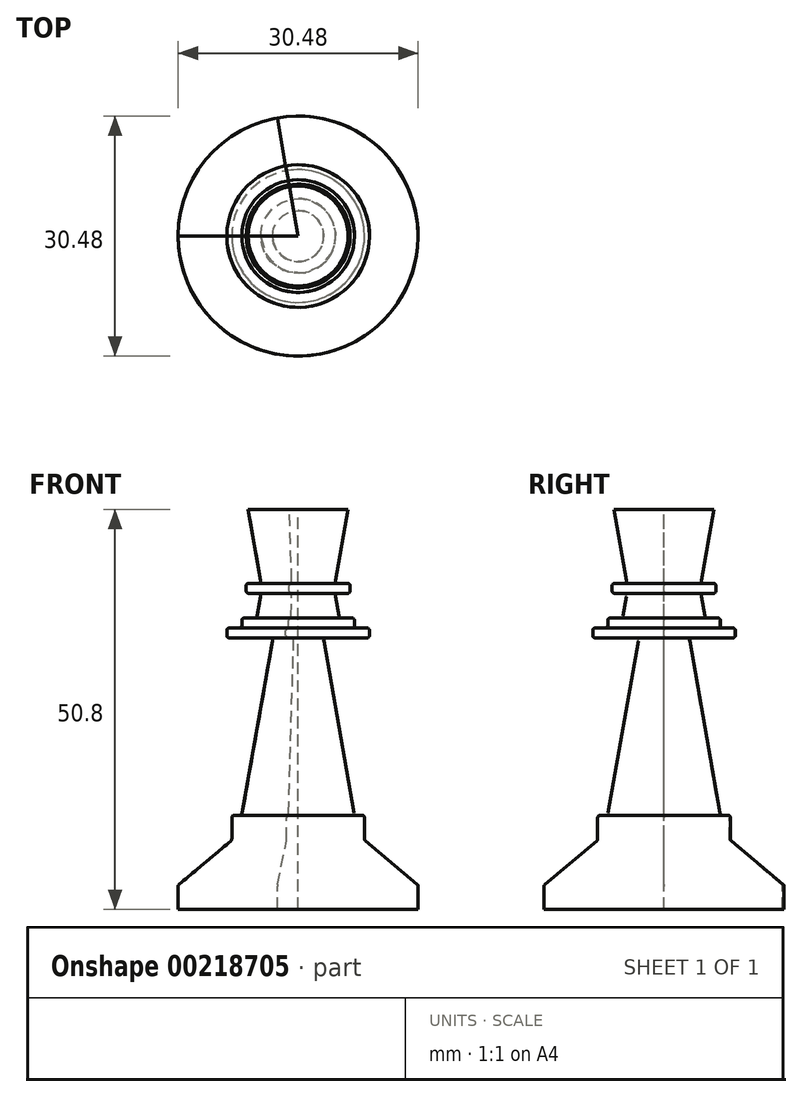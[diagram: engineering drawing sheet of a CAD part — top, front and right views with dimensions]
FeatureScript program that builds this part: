
annotation { "Feature Type Name" : "Feature", "Feature Type Description" : "" }
export const myFeature = defineFeature(function(context is Context, id is Id, definition is map)
    precondition{}
    {
        {
            var Q0;
            Q0=qCreatedBy(makeId("Front.planeOp"),FACE);
            var sketch = newSketch(context, id + "F0", { "sketchPlane" : qUnion([Q0])});
            skLineSegment(sketch, "E0.bottom", {"start": v(0, 0) * mm, "end": v(-15.24, 0) * mm});
            skLineSegment(sketch, "E0.top", {"start": v(0, 50.8) * mm, "end": v(-6.35, 50.8) * mm});
            skLineSegment(sketch, "E0.left", {"start": v(0, 0) * mm, "end": v(0, 50.8) * mm});
            skLineSegment(sketch, "E1", {"start": v(-15.24, 0) * mm, "end": v(-15.24, 2.93) * mm});
            skLineSegment(sketch, "E2", {"start": v(-15.13, 3.18) * mm, "end": v(-8.54, 8.7) * mm});
            skLineSegment(sketch, "E3", {"start": v(-8.43, 8.94) * mm, "end": v(-8.43, 11.65) * mm});
            skLineSegment(sketch, "E4", {"start": v(-8.11, 11.97) * mm, "end": v(-7.43, 11.97) * mm});
            skLineSegment(sketch, "E5", {"start": v(-7.11, 12.23) * mm, "end": v(-3.26, 34.11) * mm});
            skLineSegment(sketch, "E6", {"start": v(-3.57, 34.48) * mm, "end": v(-8.74, 34.48) * mm});
            skLineSegment(sketch, "E7", {"start": v(-9.06, 34.8) * mm, "end": v(-9.06, 35.44) * mm});
            skLineSegment(sketch, "E8", {"start": v(-8.74, 35.75) * mm, "end": v(-7.47, 35.75) * mm});
            skLineSegment(sketch, "E9", {"start": v(-7.15, 36.07) * mm, "end": v(-7.15, 36.7) * mm});
            skLineSegment(sketch, "E10", {"start": v(-6.83, 37.02) * mm, "end": v(-5.51, 37.02) * mm});
            skLineSegment(sketch, "E11", {"start": v(-5.2, 37.29) * mm, "end": v(-4.76, 39.78) * mm});
            skLineSegment(sketch, "E12", {"start": v(-5.07, 40.15) * mm, "end": v(-6.28, 40.15) * mm});
            skLineSegment(sketch, "E13", {"start": v(-6.6, 40.47) * mm, "end": v(-6.6, 41.1) * mm});
            skLineSegment(sketch, "E14", {"start": v(-6.28, 41.42) * mm, "end": v(-5.07, 41.42) * mm});
            skLineSegment(sketch, "E15", {"start": v(-4.76, 41.8) * mm, "end": v(-6.35, 50.8) * mm});
            skPoint(sketch, "E16.visualSharp", {"position": v(-15.24, 3.08) * mm});
            skArc(sketch, "E16.filletArc", {"start": v(-15.13, 3.18) * mm, "mid": v(-15.21, 3.07) * mm, "end": v(-15.24, 2.93) * mm});
            skPoint(sketch, "E17.visualSharp", {"position": v(-8.43, 8.8) * mm});
            skArc(sketch, "E17.filletArc", {"start": v(-8.54, 8.7) * mm, "mid": v(-8.46, 8.8) * mm, "end": v(-8.43, 8.94) * mm});
            skPoint(sketch, "E18.visualSharp", {"position": v(-3.2, 34.48) * mm});
            skArc(sketch, "E18.filletArc", {"start": v(-3.26, 34.11) * mm, "mid": v(-3.33, 34.37) * mm, "end": v(-3.57, 34.48) * mm});
            skPoint(sketch, "E19.visualSharp", {"position": v(-8.43, 11.97) * mm});
            skArc(sketch, "E19.filletArc", {"start": v(-8.11, 11.97) * mm, "mid": v(-8.34, 11.88) * mm, "end": v(-8.43, 11.65) * mm});
            skPoint(sketch, "E20.visualSharp", {"position": v(-7.16, 11.97) * mm});
            skArc(sketch, "E20.filletArc", {"start": v(-7.43, 11.97) * mm, "mid": v(-7.22, 12.04) * mm, "end": v(-7.11, 12.23) * mm});
            skPoint(sketch, "E21.visualSharp", {"position": v(-9.06, 34.48) * mm});
            skArc(sketch, "E21.filletArc", {"start": v(-9.06, 34.8) * mm, "mid": v(-8.96, 34.58) * mm, "end": v(-8.74, 34.48) * mm});
            skPoint(sketch, "E22.visualSharp", {"position": v(-9.06, 35.75) * mm});
            skArc(sketch, "E22.filletArc", {"start": v(-8.74, 35.75) * mm, "mid": v(-8.96, 35.66) * mm, "end": v(-9.06, 35.44) * mm});
            skPoint(sketch, "E23.visualSharp", {"position": v(-7.15, 35.75) * mm});
            skArc(sketch, "E23.filletArc", {"start": v(-7.47, 35.75) * mm, "mid": v(-7.25, 35.85) * mm, "end": v(-7.15, 36.07) * mm});
            skPoint(sketch, "E24.visualSharp", {"position": v(-7.15, 37.02) * mm});
            skArc(sketch, "E24.filletArc", {"start": v(-6.83, 37.02) * mm, "mid": v(-7.06, 36.93) * mm, "end": v(-7.15, 36.7) * mm});
            skPoint(sketch, "E25.visualSharp", {"position": v(-5.25, 37.02) * mm});
            skArc(sketch, "E25.filletArc", {"start": v(-5.51, 37.02) * mm, "mid": v(-5.3, 37.1) * mm, "end": v(-5.2, 37.29) * mm});
            skPoint(sketch, "E26.visualSharp", {"position": v(-4.7, 40.15) * mm});
            skArc(sketch, "E26.filletArc", {"start": v(-4.76, 39.78) * mm, "mid": v(-4.83, 40.04) * mm, "end": v(-5.07, 40.15) * mm});
            skPoint(sketch, "E27.visualSharp", {"position": v(-6.6, 40.15) * mm});
            skArc(sketch, "E27.filletArc", {"start": v(-6.6, 40.47) * mm, "mid": v(-6.5, 40.24) * mm, "end": v(-6.28, 40.15) * mm});
            skPoint(sketch, "E28.visualSharp", {"position": v(-6.6, 41.42) * mm});
            skArc(sketch, "E28.filletArc", {"start": v(-6.28, 41.42) * mm, "mid": v(-6.5, 41.33) * mm, "end": v(-6.6, 41.1) * mm});
            skPoint(sketch, "E29.visualSharp", {"position": v(-4.7, 41.42) * mm});
            skArc(sketch, "E29.filletArc", {"start": v(-5.07, 41.42) * mm, "mid": v(-4.83, 41.53) * mm, "end": v(-4.76, 41.8) * mm});
            skSolve(sketch);
        }
        {
            var Q0;
            Q0 = qSketchRegion(id + "F0", true);
            var Q1;
            Q1=sQuery(id+"F0.wireOp",EDGE,"E0.left");
            revolve(context, id + "F1", {"entities" : qUnion([Q0]), "axis" : qUnion([Q1]), "revolveType" : RevolveType.ONE_DIRECTION, "angle" : 280 * degree});
        }
        {
            var Q0;
            Q0=makeQuery(id+"F0.imprint","IMPRINT",FACE,{"disambiguationData":[TD([[makeQuery(id+"F0.imprint","IMPRINT",EDGE,{"derivedFrom":sQuery(id+"F0.wireOp",EDGE,"E0.bottom")}),-1.0]])]});
            var Q1;
            Q1=sQuery(id+"F0.wireOp",EDGE,"E0.left");
            revolve(context, id + "F2", {"entities" : qUnion([Q0]), "axis" : qUnion([Q1]), "revolveType" : RevolveType.FULL});
        }
    });
